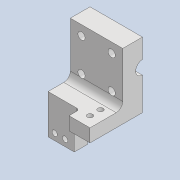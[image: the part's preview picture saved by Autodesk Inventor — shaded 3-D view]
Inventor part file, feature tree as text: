
AUTODESK INVENTOR PART (.ipt)
format: ipt  version: 2020 (Build 240168000, 168)  size: 197,120 bytes
history: native  units: mm
features: sketch x8, extrude x5, hole x3, fillet x2
ambient origin geometry x8: Origin, YZ Plane, XZ Plane, XY Plane, X Axis, Y Axis, Z Axis, Center Point
bodies: Solid1 (feature_tree)
feature tree (18):
  extrude  "Extrusion1"  Depth=40.0mm
  extrude  "Extrusion2"  Depth=15.0mm
  hole  "Hole1"  [1 undecoded]
  extrude  "Extrusion3"  Depth=8.0mm
  fillet  "Fillet2"  Radius=8.5mm
  hole  "Hole2"  [1 undecoded]
  extrude  "Extrusion4"  Depth=8.0mm
  hole  "Hole3"  [1 undecoded]
  extrude  "Extrusion5"  Depth=10.0mm
  fillet  "Fillet3"  Radius=20.0mm
  sketch  "Sketch1"  dims[d0=40.0mm d1=40.0mm]
  sketch  "Sketch2"  dims[d2=15.0mm d3=0.0mm d5=10.3mm]
  sketch  "Sketch3"  dims[d6=0.0mm d7=0.0mm d8=0.0mm]
  sketch  "Sketch4"  dims[d9=5.5mm d10=6.0mm d11=4.0mm d12=2.0mm d13=90.0deg d14=8.0mm d15=20.594885mm d20=8.5mm d21=8.5mm]
  sketch  "Sketch5"  dims[d22=40.0mm d23=10.0mm d24=0.0mm]
  sketch  "Sketch7"  dims[d25=5.0mm d26=8.0mm]
  sketch  "Sketch8"  dims[d28=4.0mm d29=6.0mm d30=4.0mm d31=2.0mm d32=90.0deg d33=8.0mm d34=20.594885mm d37=8.0mm]
  sketch  "Sketch9"  dims[d38=20.0mm d39=10.0mm d40=20.0mm d41=0.0mm d42=8.0mm d43=5.0mm d44=8.0mm d45=4.0mm d46=6.0mm d47=4.0mm d48=2.0mm d49=90.0deg d50=8.0mm d51=20.594885mm d52=8.0mm d53=15.0mm d54=0.0mm d55=2.0mm d56=5.0mm]
note: 3 required parameter values undecoded (feature->parameter linkage not recoverable at this tier; creation-order binding heuristic only, values carry confidence <= 0.55)
